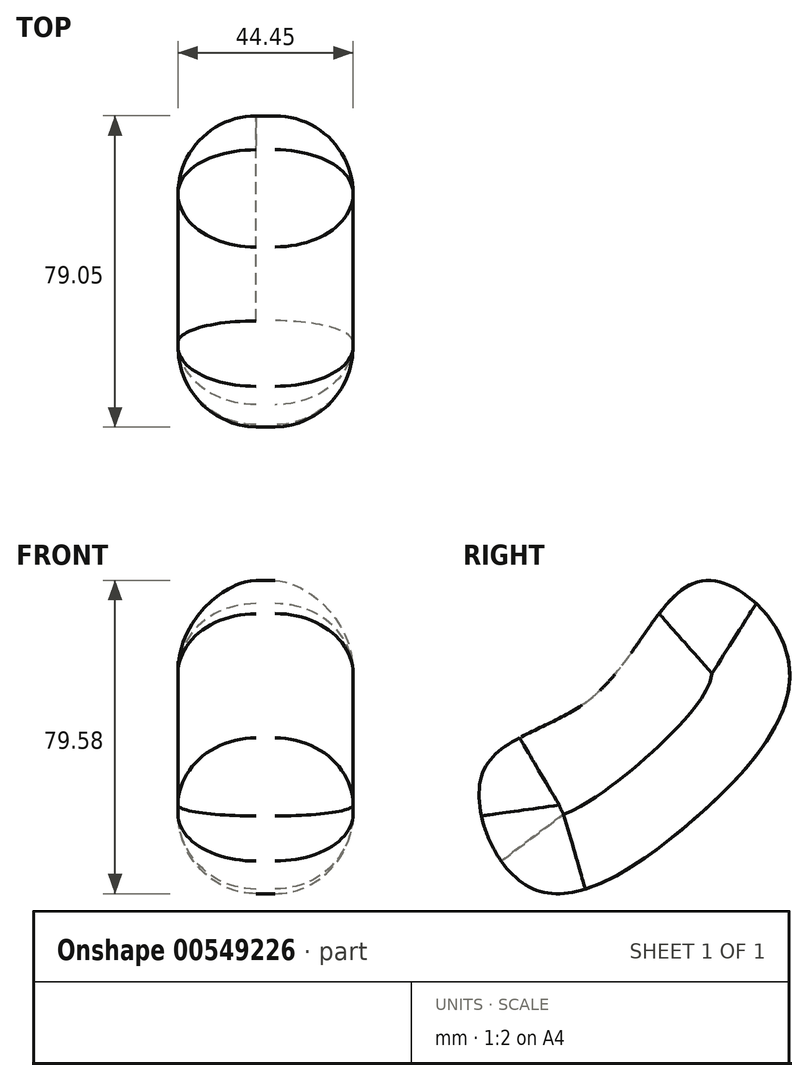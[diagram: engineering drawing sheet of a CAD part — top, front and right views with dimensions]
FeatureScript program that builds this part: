
annotation { "Feature Type Name" : "Feature", "Feature Type Description" : "" }
export const myFeature = defineFeature(function(context is Context, id is Id, definition is map)
    precondition{}
    {
        {
            var Q0;
            Q0=qCreatedBy(makeId("Right.planeOp"),FACE);
            var sketch = newSketch(context, id + "F0", { "sketchPlane" : qUnion([Q0])});
            skFitSpline(sketch, "E0", {"points": [v(0, 0) * mm, v(41.24, 17.3) * mm, v(65.47, 57.9) * mm, v(43.18, 77.96) * mm, v(16.2, 48.97) * mm, v(-12.19, 29.5) * mm, v(0, 0) * mm]});
            skSolve(sketch);
        }
        {
            var Q0;
            Q0 = qSketchRegion(id + "F0", true);
            extrude(context, id + "F1", {"entities" : qUnion([Q0]), "depth" : 44.45 * mm, "offsetDistance" : 25.4 * mm});
        }
        {
            var Q0;
            Q0=makeQuery(id+"F1.opExtrude","CAP_FACE",FACE,{"disambiguationData":[OSD([sQuery(id+"F0.wireOp",EDGE,"E0")])],"isStart":false});
            var Q1;
            Q1=makeQuery(id+"F1.opExtrude","CAP_FACE",FACE,{"disambiguationData":[OSD([sQuery(id+"F0.wireOp",EDGE,"E0")])],"isStart":true});
            fillet(context, id + "F2", {"entities" : qUnion([Q0, Q1]), "radius" : 19.8 * mm, "allowEdgeOverflow" : false});
        }
    });
